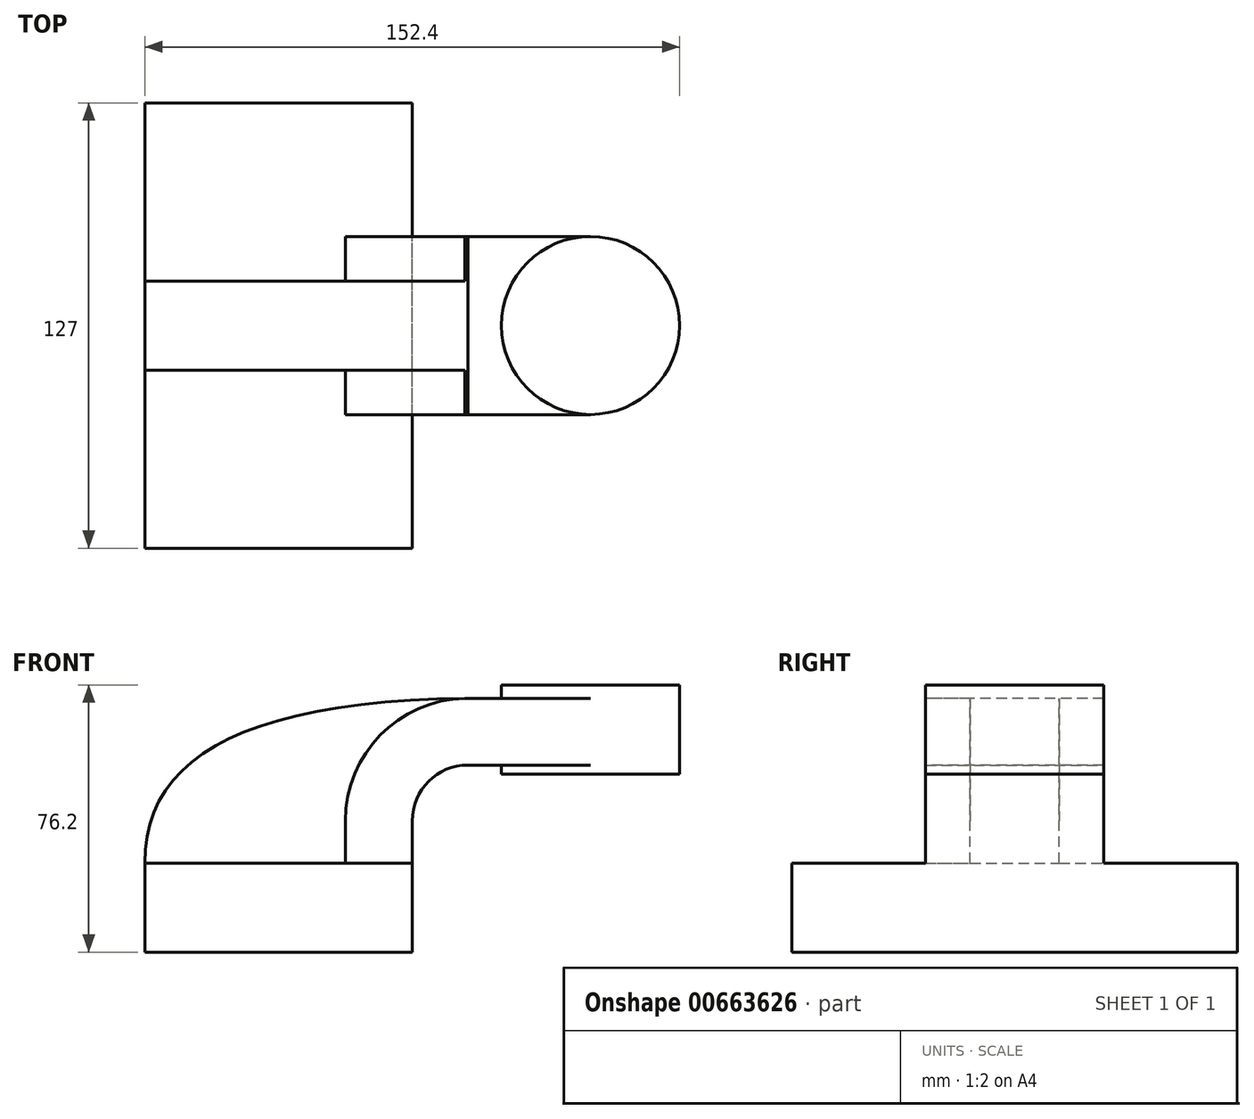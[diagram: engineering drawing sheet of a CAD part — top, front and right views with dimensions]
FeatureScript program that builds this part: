
annotation { "Feature Type Name" : "Feature", "Feature Type Description" : "" }
export const myFeature = defineFeature(function(context is Context, id is Id, definition is map)
    precondition{}
    {
        {
            var Q0;
            Q0=qCreatedBy(makeId("Front.planeOp"),FACE);
            var sketch = newSketch(context, id + "F0", { "sketchPlane" : qUnion([Q0])});
            skLineSegment(sketch, "E0.bottom", {"start": v(38.1, 12.7) * mm, "end": v(-38.1, 12.7) * mm});
            skLineSegment(sketch, "E0.top", {"start": v(38.1, -12.7) * mm, "end": v(-38.1, -12.7) * mm});
            skLineSegment(sketch, "E0.left", {"start": v(38.1, 12.7) * mm, "end": v(38.1, -12.7) * mm});
            skLineSegment(sketch, "E0.right", {"start": v(-38.1, 12.7) * mm, "end": v(-38.1, -12.7) * mm});
            skPoint(sketch, "E0.middle", {"position": v(0, 0) * mm});
            skLineSegment(sketch, "E1.bottom", {"start": v(63.5, 63.5) * mm, "end": v(114.3, 63.5) * mm});
            skLineSegment(sketch, "E1.top", {"start": v(63.5, 38.1) * mm, "end": v(114.3, 38.1) * mm});
            skLineSegment(sketch, "E1.left", {"start": v(63.5, 63.5) * mm, "end": v(63.5, 38.1) * mm});
            skLineSegment(sketch, "E1.right", {"start": v(114.3, 63.5) * mm, "end": v(114.3, 38.1) * mm});
            skPoint(sketch, "E1.middle", {"position": v(88.9, 50.8) * mm});
            skLineSegment(sketch, "E2", {"start": v(38.1, 12.7) * mm, "end": v(38.1, 24.77) * mm});
            skArc(sketch, "E3", {"start": v(38.1, 24.77) * mm, "mid": v(42.75, 36) * mm, "end": v(53.97, 40.64) * mm});
            skLineSegment(sketch, "E4", {"start": v(53.97, 40.64) * mm, "end": v(105.18, 40.64) * mm});
            skLineSegment(sketch, "E5.0", {"start": v(53.97, 59.7) * mm, "end": v(105.18, 59.7) * mm});
            skArc(sketch, "E5.1", {"start": v(19.05, 24.77) * mm, "mid": v(29.28, 49.46) * mm, "end": v(53.97, 59.7) * mm});
            skLineSegment(sketch, "E5.2", {"start": v(19.05, 12.7) * mm, "end": v(19.05, 24.77) * mm});
            skFitSpline(sketch, "E6", {"points": [v(-38.1, 12.7) * mm, v(53.97, 59.7) * mm], "startDerivative": vector(-1.1, 90.63) * mm, "endDerivative": vector(189.18, 2.04) * mm});
            skLineSegment(sketch, "E7", {"start": v(88.9, 63.5) * mm, "end": v(88.9, 38.1) * mm});
            skSolve(sketch);
        }
        {
            var Q0;
            Q0=makeQuery(id+"F0.imprint","IMPRINT",FACE,{"disambiguationData":[TD([[makeQuery(id+"F0.imprint","IMPRINT",EDGE,{"derivedFrom":sQuery(id+"F0.wireOp",EDGE,"E0.top")}),-1.0]])]});
            extrude(context, id + "F1", {"entities" : qUnion([Q0]), "endBound" : BoundingType.SYMMETRIC, "depth" : 127 * mm, "offsetDistance" : 25.4 * mm});
        }
        {
            var Q0;
            {var subQ3=sQuery(id+"F0.wireOp",EDGE,"E5.2");Q0=makeQuery(id+"F0.imprint","IMPRINT",FACE,{"disambiguationData":[TD([[makeQuery(id+"F0.imprint","IMPRINT",EDGE,{"derivedFrom":subQ3}),1.0]])]});}
            extrude(context, id + "F2", {"entities" : qUnion([Q0]), "operationType" : NewBodyOperationType.ADD, "endBound" : BoundingType.SYMMETRIC, "depth" : 25.4 * mm, "offsetDistance" : 25.4 * mm});
        }
        {
            var Q0;
            {var subQ1=sQuery(id+"F0.wireOp",EDGE,"E2");Q0=makeQuery(id+"F0.imprint","IMPRINT",FACE,{"disambiguationData":[TD([[makeQuery(id+"F0.imprint","IMPRINT",EDGE,{"derivedFrom":subQ1}),1.0]])]});}
            var Q1;
            {var subQ0=sQuery(id+"F0.wireOp",EDGE,"E5.0");var subQ1=sQuery(id+"F0.wireOp",EDGE,"E1.left");var subQ2=makeQuery(id+"F0.imprint","INTERSECT",VERTEX,{"derivedFrom":[subQ1,subQ0]});Q1=makeQuery(id+"F0.imprint","IMPRINT",FACE,{"disambiguationData":[TD([[makeQuery(id+"F0.imprint","IMPRINT",EDGE,{"disambiguationData":[TD([[subQ2,-1.0]])],"derivedFrom":subQ1}),1.0]])]});}
            extrude(context, id + "F3", {"entities" : qUnion([Q0, Q1]), "operationType" : NewBodyOperationType.ADD, "endBound" : BoundingType.SYMMETRIC, "depth" : 50.8 * mm, "offsetDistance" : 25.4 * mm});
        }
        {
            var Q0;
            {var subQ4=sQuery(id+"F0.wireOp",EDGE,"E1.right");Q0=makeQuery(id+"F0.imprint","IMPRINT",FACE,{"disambiguationData":[TD([[makeQuery(id+"F0.imprint","IMPRINT",EDGE,{"derivedFrom":subQ4}),-1.0]])]});}
            var Q1;
            Q1=sQuery(id+"F0.wireOp",EDGE,"E7");
            revolve(context, id + "F4", {"operationType" : NewBodyOperationType.ADD, "entities" : qUnion([Q0]), "axis" : qUnion([Q1]), "revolveType" : RevolveType.FULL});
        }
    });
